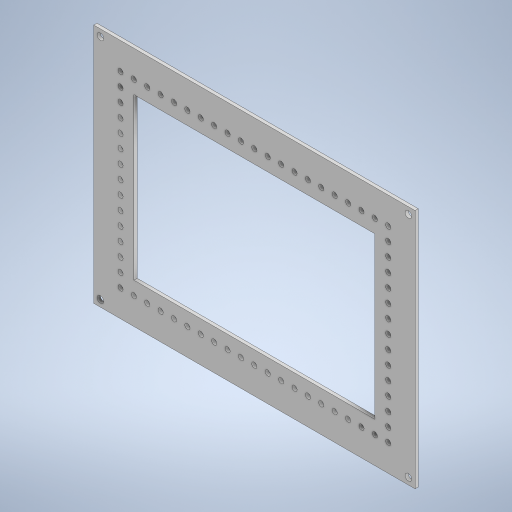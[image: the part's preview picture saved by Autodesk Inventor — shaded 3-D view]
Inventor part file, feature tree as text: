
AUTODESK INVENTOR PART (.ipt)
format: ipt  version: 2023.4 (Build 274418000, 418)  size: 387,584 bytes
history: native  units: in
note: dims shown in document units (in); Inventor stores cm internally (conversion verified against a paired STEP export)
features: sketch x3, extrude x2, sheet_metal_op x1, other x1
ambient origin geometry x8: Origin, YZ Plane, XZ Plane, XY Plane, X Axis, Y Axis, Z Axis, Center Point
bodies: Solid1 (feature_tree)
feature tree (7):
  sheet_metal_op  "Face1"
  extrude  "Extrusion1"  Depth=6.0in
  extrude  "Extrusion2"  Depth=0.12in
  sketch  "Sketch1"  dims[d0=9.0in d1=6.0in]
  other  "Plate1"
  sketch  "Sketch2"  dims[d2=1.5in d3=0.12in]
  sketch  "Sketch3"  dims[d4=0.197in d6=0.5in d7=0.5in d8=7.874in d10=0.5in d11=0.3937in d13=1.0in d15=1.0in d16=0.0in d17=0.197in d18=1.0in d19=0.5in d20=5.5118in d22=0.5in d23=0.3937in d25=1.0in d27=0.197in d30=1.0in d31=0.5in d32=7.874in d34=0.5in d35=0.3937in d37=1.0in d39=0.197in d40=1.0in d41=0.5in d42=5.5118in d44=0.5in d45=0.3937in d47=1.0in d49=0.25in d50=0.25in d51=0.25in d52=0.25in d53=0.25in d54=0.25in d55=0.25in d56=0.25in d57=0.25in d58=0.25in d59=0.25in d60=0.25in d61=1.0in d62=0.0in]
